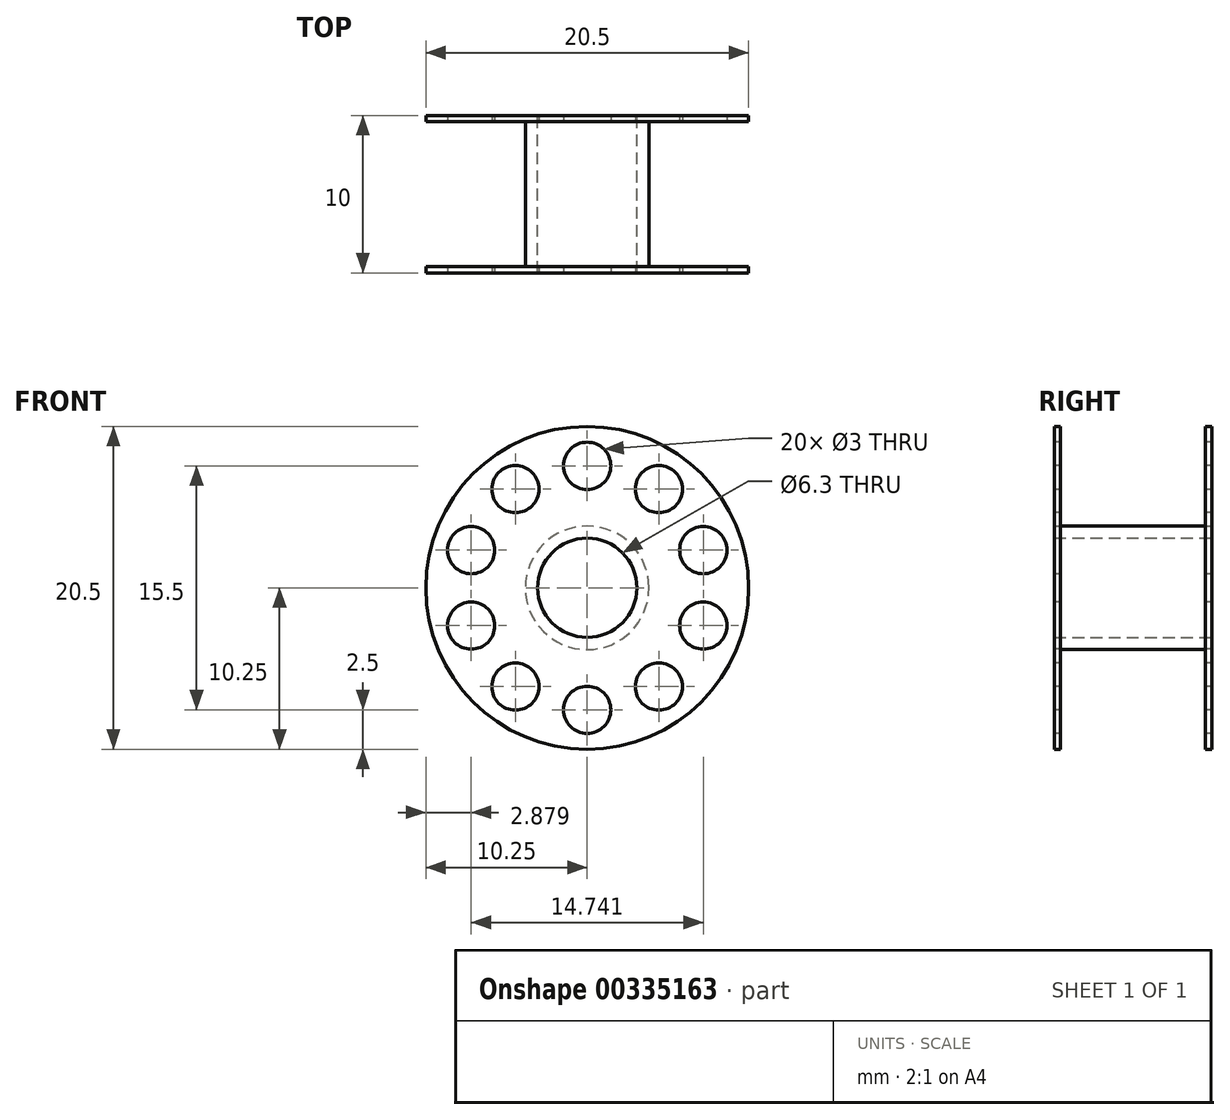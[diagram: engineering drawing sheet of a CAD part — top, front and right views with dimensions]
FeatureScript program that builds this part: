
annotation { "Feature Type Name" : "Feature", "Feature Type Description" : "" }
export const myFeature = defineFeature(function(context is Context, id is Id, definition is map)
    precondition{}
    {
        {
            var Q0;
            Q0=qCreatedBy(makeId("Front.planeOp"),FACE);
            var sketch = newSketch(context, id + "F0", { "sketchPlane" : qUnion([Q0])});
            skCircle(sketch, "E0", {"center": v(0, 0) * mm, "radius": 10.25 * mm});
            skCircle(sketch, "E1", {"center": v(0, 0) * mm, "radius": 3.15 * mm});
            skCircle(sketch, "E2", {"center": v(0, 0) * mm, "radius": 3.92 * mm});
            skSolve(sketch);
        }
        {
            var Q0;
            Q0=makeQuery(id+"F0.imprint","IMPRINT",FACE,{"disambiguationData":[TD([[makeQuery(id+"F0.imprint","IMPRINT",EDGE,{"derivedFrom":sQuery(id+"F0.wireOp",EDGE,"E0")}),1.0]])]});
            var Q1;
            Q1=makeQuery(id+"F0.imprint","IMPRINT",FACE,{"disambiguationData":[TD([[makeQuery(id+"F0.imprint","IMPRINT",EDGE,{"derivedFrom":sQuery(id+"F0.wireOp",EDGE,"E1")}),-1.0]])]});
            extrude(context, id + "F1", {"entities" : qUnion([Q0, Q1]), "endBound" : BoundingType.SYMMETRIC, "depth" : 10 * mm});
        }
        {
            var Q0;
            Q0=qSketchRegion(id+"F0",true);
            extrude(context, id + "F2", {"entities" : qUnion([Q0]), "operationType" : NewBodyOperationType.REMOVE, "endBound" : BoundingType.SYMMETRIC, "oppositeDirection" : true, "depth" : 9.2 * mm});
        }
        {
            var Q0;
            Q0=makeQuery(id+"F1.opExtrude","CAP_FACE",FACE,{"disambiguationData":[OSD([sQuery(id+"F0.wireOp",EDGE,"E0"),sQuery(id+"F0.wireOp",EDGE,"E1")])],"isStart":false});
            var sketch = newSketch(context, id + "F3", { "sketchPlane" : qUnion([Q0])});
            skPoint(sketch, "E3", {"position": v(0, 9.25) * mm});
            skCircle(sketch, "E4", {"center": v(0, 7.75) * mm, "radius": 1.5 * mm});
            skSolve(sketch);
        }
        {
            var Q0;
            Q0=makeQuery(id+"F3.imprint","IMPRINT",FACE,{"disambiguationData":[TD([[makeQuery(id+"F3.imprint","IMPRINT",EDGE,{"derivedFrom":sQuery(id+"F3.wireOp",EDGE,"E4")}),1.0]])]});
            extrude(context, id + "F4", {"entities" : qUnion([Q0]), "endBound" : BoundingType.SYMMETRIC, "oppositeDirection" : true, "depth" : 25 * mm});
        }
        {
            var Q0;
            Q0=makeQuery(id+"F4.opExtrude","SWEPT_BODY",BODY,{"disambiguationData":[OSD([sQuery(id+"F3.wireOp",EDGE,"E4")])]});
            var Q1;
            Q1=makeQuery(id+"F1.opExtrude","CAP_EDGE",EDGE,{"disambiguationData":[OSD([sQuery(id+"F0.wireOp",EDGE,"E1")])],"isStart":false});
            circularPattern(context, id + "F5", {"entities" : qUnion([Q0]), "axis" : qUnion([Q1]), "angle" : 36 * degree, "instanceCount" : 10});
        }
        {
            var Q0;
            Q0=makeQuery(id+"F4.opExtrude","SWEPT_BODY",BODY,{"disambiguationData":[OSD([sQuery(id+"F3.wireOp",EDGE,"E4")])]});
            var Q1;
            Q1=makeQuery(id+"F5.opPattern","COPY",BODY,{"derivedFrom":makeQuery(id+"F4.opExtrude","SWEPT_BODY",BODY,{"disambiguationData":[OSD([sQuery(id+"F3.wireOp",EDGE,"E4")])]}),"instanceName":"1"});
            var Q2;
            Q2=makeQuery(id+"F5.opPattern","COPY",BODY,{"derivedFrom":makeQuery(id+"F4.opExtrude","SWEPT_BODY",BODY,{"disambiguationData":[OSD([sQuery(id+"F3.wireOp",EDGE,"E4")])]}),"instanceName":"2"});
            var Q3;
            Q3=makeQuery(id+"F5.opPattern","COPY",BODY,{"derivedFrom":makeQuery(id+"F4.opExtrude","SWEPT_BODY",BODY,{"disambiguationData":[OSD([sQuery(id+"F3.wireOp",EDGE,"E4")])]}),"instanceName":"3"});
            var Q4;
            Q4=makeQuery(id+"F5.opPattern","COPY",BODY,{"derivedFrom":makeQuery(id+"F4.opExtrude","SWEPT_BODY",BODY,{"disambiguationData":[OSD([sQuery(id+"F3.wireOp",EDGE,"E4")])]}),"instanceName":"4"});
            var Q5;
            Q5=makeQuery(id+"F5.opPattern","COPY",BODY,{"derivedFrom":makeQuery(id+"F4.opExtrude","SWEPT_BODY",BODY,{"disambiguationData":[OSD([sQuery(id+"F3.wireOp",EDGE,"E4")])]}),"instanceName":"5"});
            var Q6;
            Q6=makeQuery(id+"F5.opPattern","COPY",BODY,{"derivedFrom":makeQuery(id+"F4.opExtrude","SWEPT_BODY",BODY,{"disambiguationData":[OSD([sQuery(id+"F3.wireOp",EDGE,"E4")])]}),"instanceName":"6"});
            var Q7;
            Q7=makeQuery(id+"F5.opPattern","COPY",BODY,{"derivedFrom":makeQuery(id+"F4.opExtrude","SWEPT_BODY",BODY,{"disambiguationData":[OSD([sQuery(id+"F3.wireOp",EDGE,"E4")])]}),"instanceName":"7"});
            var Q8;
            Q8=makeQuery(id+"F5.opPattern","COPY",BODY,{"derivedFrom":makeQuery(id+"F4.opExtrude","SWEPT_BODY",BODY,{"disambiguationData":[OSD([sQuery(id+"F3.wireOp",EDGE,"E4")])]}),"instanceName":"8"});
            var Q9;
            Q9=makeQuery(id+"F5.opPattern","COPY",BODY,{"derivedFrom":makeQuery(id+"F4.opExtrude","SWEPT_BODY",BODY,{"disambiguationData":[OSD([sQuery(id+"F3.wireOp",EDGE,"E4")])]}),"instanceName":"9"});
            var Q10;
            Q10=makeQuery(id+"F1.opExtrude","SWEPT_BODY",BODY,{"disambiguationData":[OSD([sQuery(id+"F0.wireOp",EDGE,"E0"),sQuery(id+"F0.wireOp",EDGE,"E1")])]});
            booleanBodies(context, id + "F6", {"operationType" : BooleanOperationType.SUBTRACTION, "tools" : qUnion([Q0, Q1, Q2, Q3, Q4, Q5, Q6, Q7, Q8, Q9]), "targets" : qUnion([Q10])});
        }
    });
